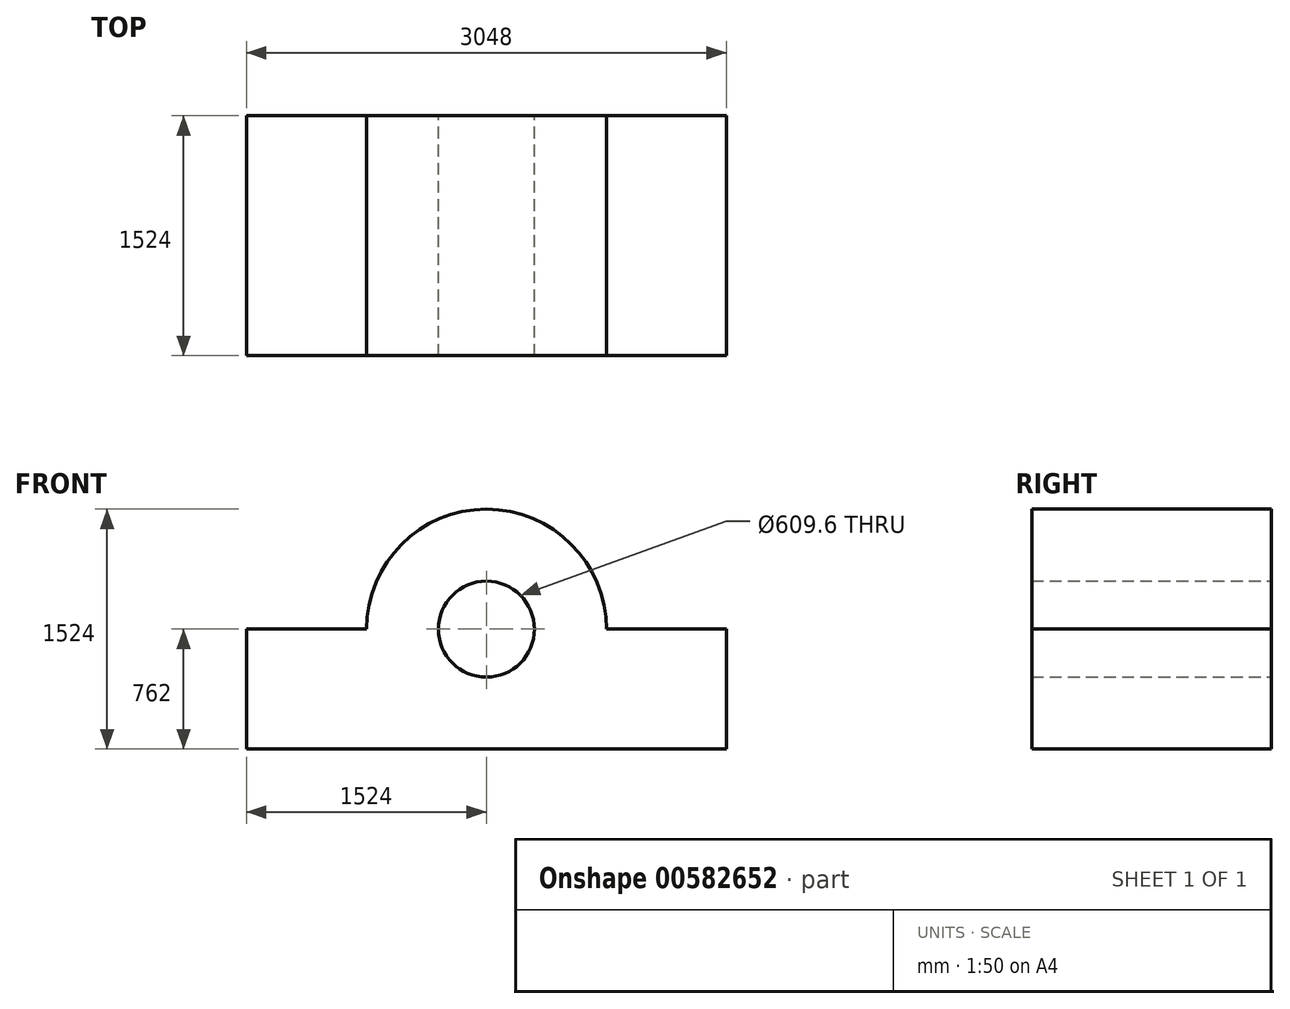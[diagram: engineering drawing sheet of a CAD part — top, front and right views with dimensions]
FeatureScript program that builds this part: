
annotation { "Feature Type Name" : "Feature", "Feature Type Description" : "" }
export const myFeature = defineFeature(function(context is Context, id is Id, definition is map)
    precondition{}
    {
        {
            var Q0;
            Q0=qCreatedBy(makeId("Front.planeOp"),FACE);
            var sketch = newSketch(context, id + "F0", { "sketchPlane" : qUnion([Q0])});
            skLineSegment(sketch, "E0", {"start": v(0, 0) * mm, "end": v(3048, 0) * mm});
            skLineSegment(sketch, "E1", {"start": v(3048, 0) * mm, "end": v(3048, 762) * mm});
            skLineSegment(sketch, "E2", {"start": v(0, 0) * mm, "end": v(0, 762) * mm});
            skLineSegment(sketch, "E3", {"start": v(0, 762) * mm, "end": v(762, 762) * mm});
            skArc(sketch, "E4", {"start": v(2286, 762) * mm, "mid": v(1524, 1524) * mm, "end": v(762, 762) * mm});
            skCircle(sketch, "E5", {"center": v(1524, 762) * mm, "radius": 304.8 * mm});
            skLineSegment(sketch, "E6.trimOffspring", {"start": v(2286, 762) * mm, "end": v(3048, 762) * mm});
            skSolve(sketch);
        }
        {
            var Q0;
            Q0 = qSketchRegion(id + "F0", true);
            extrude(context, id + "F1", {"entities" : qUnion([Q0]), "depth" : 1524 * mm, "offsetDistance" : 25.4 * mm});
        }
    });
